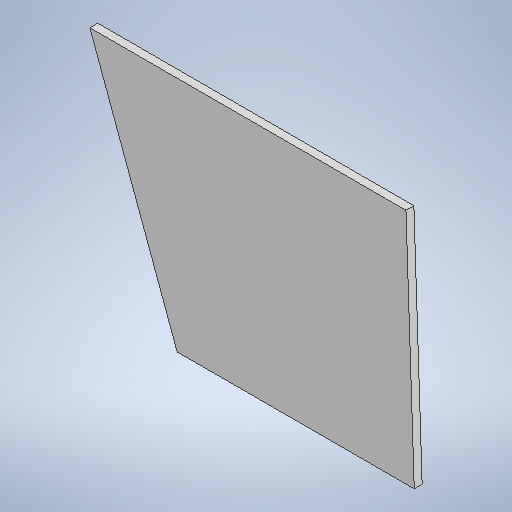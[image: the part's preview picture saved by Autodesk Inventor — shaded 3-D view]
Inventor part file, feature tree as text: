
AUTODESK INVENTOR PART (.ipt)
format: ipt  version: 2025 (Build 290162010, 162A)  size: 230,912 bytes
history: native  units: mm
features: sheet_metal_op x1, sketch x1, other x1
ambient origin geometry x8: Origin, YZ Plane, XZ Plane, XY Plane, X Axis, Y Axis, Z Axis, Center Point
bodies: Body1 (feature_tree)
feature tree (3):
  sheet_metal_op  "Face2"
  sketch  "Sketch5"  dims[d26=400.0mm d27=0.349066mm d28=300.0mm d29=300.0mm d30=10.0mm]
  other  "Plate3"
